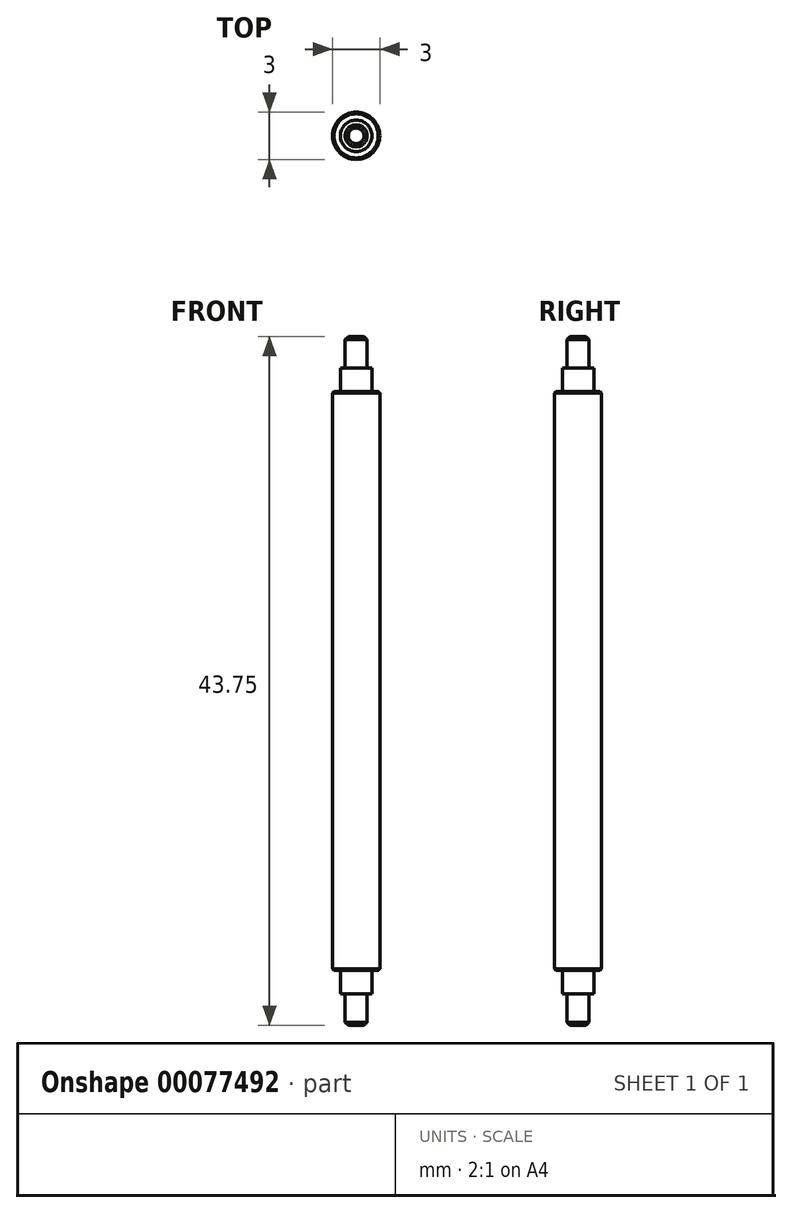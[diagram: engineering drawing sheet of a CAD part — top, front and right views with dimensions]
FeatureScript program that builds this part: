
annotation { "Feature Type Name" : "Feature", "Feature Type Description" : "" }
export const myFeature = defineFeature(function(context is Context, id is Id, definition is map)
    precondition{}
    {
        {
            var Q0;
            Q0=qCreatedBy(makeId("Top.planeOp"),FACE);
            var sketch = newSketch(context, id + "F0", { "sketchPlane" : qUnion([Q0])});
            skCircle(sketch, "E0", {"center": v(0, 0) * mm, "radius": 0.7 * mm});
            skSolve(sketch);
        }
        {
            var Q0;
            Q0=makeQuery(id+"F0.imprint","IMPRINT",FACE,{"disambiguationData":[TD([[makeQuery(id+"F0.imprint","IMPRINT",EDGE,{"derivedFrom":sQuery(id+"F0.wireOp",EDGE,"E0")}),1.0]])]});
            extrude(context, id + "F1", {"entities" : qUnion([Q0]), "depth" : 2 * mm});
        }
        {
            var Q0;
            Q0=makeQuery(id+"F1.opExtrude","CAP_FACE",FACE,{"disambiguationData":[OSD([sQuery(id+"F0.wireOp",EDGE,"E0")])],"isStart":false});
            var sketch = newSketch(context, id + "F2", { "sketchPlane" : qUnion([Q0])});
            skCircle(sketch, "E1", {"center": v(0, 0) * mm, "radius": 1 * mm});
            skSolve(sketch);
        }
        {
            var Q0;
            {var subQ0=makeQuery(id+"F2.imprint","IMPRINT",EDGE,{"derivedFrom":makeQuery(id+"F1.opExtrude","CAP_EDGE",EDGE,{"disambiguationData":[OSD([sQuery(id+"F0.wireOp",EDGE,"E0")])],"isStart":false})});Q0=qUnion([makeQuery(id+"F2.imprint","IMPRINT",FACE,{"disambiguationData":[TD([[makeQuery(id+"F2.imprint","IMPRINT",EDGE,{"derivedFrom":sQuery(id+"F2.wireOp",EDGE,"E1")}),1.0]])]}),makeQuery(id+"F2.imprint","IMPRINT",FACE,{"disambiguationData":[TD([[subQ0,1.0]])]})]);}
            extrude(context, id + "F3", {"entities" : qUnion([Q0]), "operationType" : NewBodyOperationType.ADD, "depth" : 1.5 * mm});
        }
        {
            var Q0;
            Q0=makeQuery(id+"F3.opExtrude","CAP_FACE",FACE,{"disambiguationData":[OSD([sQuery(id+"F2.wireOp",EDGE,"E1")])],"isStart":false});
            var sketch = newSketch(context, id + "F4", { "sketchPlane" : qUnion([Q0])});
            skCircle(sketch, "E2", {"center": v(0, 0) * mm, "radius": 1.5 * mm});
            skSolve(sketch);
        }
        {
            var Q0;
            {var subQ0=makeQuery(id+"F4.imprint","IMPRINT",EDGE,{"derivedFrom":makeQuery(id+"F3.opExtrude","CAP_EDGE",EDGE,{"disambiguationData":[OSD([sQuery(id+"F2.wireOp",EDGE,"E1")])],"isStart":false})});Q0=qUnion([makeQuery(id+"F4.imprint","IMPRINT",FACE,{"disambiguationData":[TD([[makeQuery(id+"F4.imprint","IMPRINT",EDGE,{"derivedFrom":sQuery(id+"F4.wireOp",EDGE,"E2")}),1.0]])]}),makeQuery(id+"F4.imprint","IMPRINT",FACE,{"disambiguationData":[TD([[subQ0,1.0]])]})]);}
            extrude(context, id + "F5", {"entities" : qUnion([Q0]), "operationType" : NewBodyOperationType.ADD, "depth" : 36.75 * mm});
        }
        {
            var Q0;
            Q0=makeQuery(id+"F5.opExtrude","CAP_FACE",FACE,{"disambiguationData":[OSD([sQuery(id+"F4.wireOp",EDGE,"E2")])],"isStart":false});
            var sketch = newSketch(context, id + "F6", { "sketchPlane" : qUnion([Q0])});
            skCircle(sketch, "E3", {"center": v(0, 0) * mm, "radius": 1 * mm});
            skSolve(sketch);
        }
        {
            var Q0;
            Q0=makeQuery(id+"F6.imprint","IMPRINT",FACE,{"disambiguationData":[TD([[makeQuery(id+"F6.imprint","IMPRINT",EDGE,{"derivedFrom":sQuery(id+"F6.wireOp",EDGE,"E3")}),1.0]])]});
            extrude(context, id + "F7", {"entities" : qUnion([Q0]), "operationType" : NewBodyOperationType.ADD, "depth" : 1.5 * mm});
        }
        {
            var Q0;
            Q0=makeQuery(id+"F7.opExtrude","CAP_FACE",FACE,{"disambiguationData":[OSD([sQuery(id+"F6.wireOp",EDGE,"E3")])],"isStart":false});
            var sketch = newSketch(context, id + "F8", { "sketchPlane" : qUnion([Q0])});
            skCircle(sketch, "E4", {"center": v(0, 0) * mm, "radius": 0.7 * mm});
            skSolve(sketch);
        }
        {
            var Q0;
            Q0=makeQuery(id+"F8.imprint","IMPRINT",FACE,{"disambiguationData":[TD([[makeQuery(id+"F8.imprint","IMPRINT",EDGE,{"derivedFrom":sQuery(id+"F8.wireOp",EDGE,"E4")}),1.0]])]});
            extrude(context, id + "F9", {"entities" : qUnion([Q0]), "operationType" : NewBodyOperationType.ADD, "depth" : 2 * mm});
        }
        {
            var Q0;
            Q0=makeQuery(id+"F1.opExtrude","CAP_EDGE",EDGE,{"disambiguationData":[OSD([sQuery(id+"F0.wireOp",EDGE,"E0")])],"isStart":true});
            var Q1;
            Q1=makeQuery(id+"F9.opExtrude","CAP_EDGE",EDGE,{"disambiguationData":[OSD([sQuery(id+"F8.wireOp",EDGE,"E4")])],"isStart":false});
            chamfer(context, id + "F10", {"entities" : qUnion([Q0, Q1]), "width" : 0.2 * mm, "tangentPropagation" : true});
        }
        {
            var Q0;
            Q0=makeQuery(id+"F5.opExtrude","CAP_EDGE",EDGE,{"disambiguationData":[OSD([sQuery(id+"F4.wireOp",EDGE,"E2")])],"isStart":false});
            var Q1;
            Q1=makeQuery(id+"F5.opExtrude","CAP_EDGE",EDGE,{"disambiguationData":[OSD([sQuery(id+"F4.wireOp",EDGE,"E2")])],"isStart":true});
            chamfer(context, id + "F11", {"entities" : qUnion([Q0, Q1]), "width" : 0.1 * mm, "tangentPropagation" : true});
        }
    });
